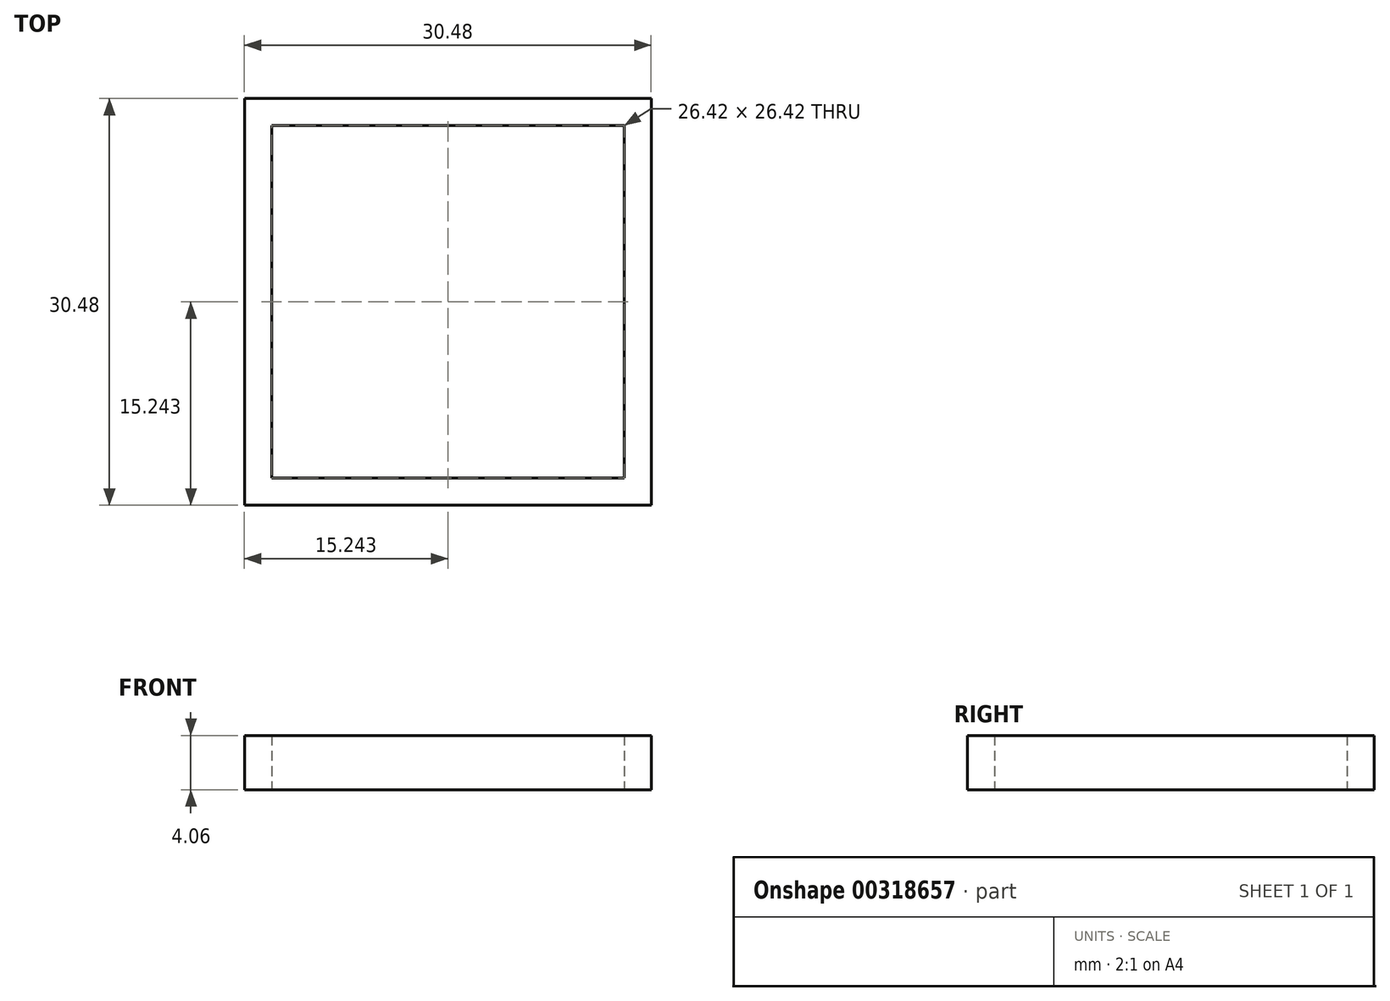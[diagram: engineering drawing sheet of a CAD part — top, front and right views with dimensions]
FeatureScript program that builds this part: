
annotation { "Feature Type Name" : "Feature", "Feature Type Description" : "" }
export const myFeature = defineFeature(function(context is Context, id is Id, definition is map)
    precondition{}
    {
        {
            var Q0;
            Q0=qCreatedBy(makeId("Top.planeOp"),FACE);
            var sketch = newSketch(context, id + "F0", { "sketchPlane" : qUnion([Q0])});
            skLineSegment(sketch, "E0.bottom", {"start": v(-35.39, -24.63) * mm, "end": v(-4.9, -24.63) * mm});
            skLineSegment(sketch, "E0.top", {"start": v(-35.39, -26.66) * mm, "end": v(-4.9, -26.66) * mm});
            skLineSegment(sketch, "E0.left", {"start": v(-35.39, -24.63) * mm, "end": v(-35.39, -26.66) * mm});
            skLineSegment(sketch, "E0.right", {"start": v(-4.9, -24.63) * mm, "end": v(-4.9, -26.66) * mm});
            skLineSegment(sketch, "E1.bottom", {"start": v(-35.39, -24.63) * mm, "end": v(-33.35, -24.63) * mm});
            skLineSegment(sketch, "E1.top", {"start": v(-35.39, 1.8) * mm, "end": v(-33.35, 1.8) * mm});
            skLineSegment(sketch, "E1.left", {"start": v(-35.39, -24.63) * mm, "end": v(-35.39, 1.8) * mm});
            skLineSegment(sketch, "E1.right", {"start": v(-33.35, -24.63) * mm, "end": v(-33.35, 1.8) * mm});
            skLineSegment(sketch, "E2.bottom", {"start": v(-4.9, -24.63) * mm, "end": v(-6.94, -24.63) * mm});
            skLineSegment(sketch, "E2.top", {"start": v(-4.9, 1.8) * mm, "end": v(-6.94, 1.8) * mm});
            skLineSegment(sketch, "E2.left", {"start": v(-4.9, -24.63) * mm, "end": v(-4.9, 1.8) * mm});
            skLineSegment(sketch, "E2.right", {"start": v(-6.94, -24.63) * mm, "end": v(-6.94, 1.8) * mm});
            skLineSegment(sketch, "E3.bottom", {"start": v(-35.39, 1.8) * mm, "end": v(-4.9, 1.8) * mm});
            skLineSegment(sketch, "E3.top", {"start": v(-35.39, 3.82) * mm, "end": v(-4.9, 3.82) * mm});
            skLineSegment(sketch, "E3.left", {"start": v(-35.39, 1.8) * mm, "end": v(-35.39, 3.82) * mm});
            skLineSegment(sketch, "E3.right", {"start": v(-4.9, 1.8) * mm, "end": v(-4.9, 3.82) * mm});
            skSolve(sketch);
        }
        {
            var Q0;
            Q0 = qSketchRegion(id + "F0", true);
            extrude(context, id + "F1", {"entities" : qUnion([Q0]), "depth" : 4.06 * mm});
        }
    });
